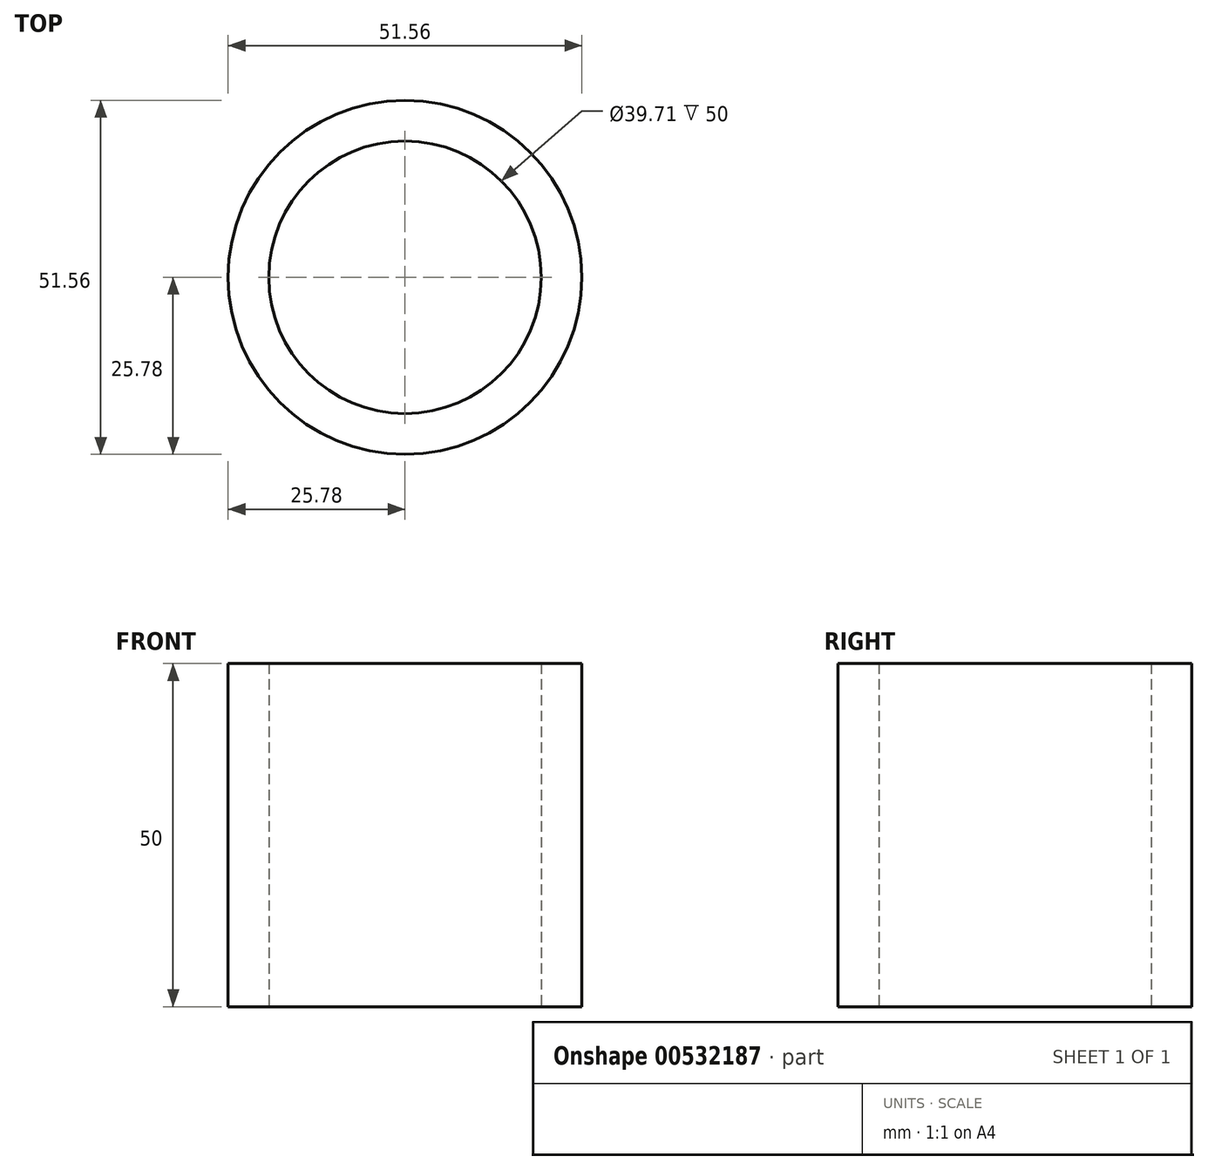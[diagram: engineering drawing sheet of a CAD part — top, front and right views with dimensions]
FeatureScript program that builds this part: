
annotation { "Feature Type Name" : "Feature", "Feature Type Description" : "" }
export const myFeature = defineFeature(function(context is Context, id is Id, definition is map)
    precondition{}
    {
        {
            var Q0;
            Q0=qCreatedBy(makeId("Top.planeOp"),FACE);
            var sketch = newSketch(context, id + "F0", { "sketchPlane" : qUnion([Q0])});
            skCircle(sketch, "E0", {"center": v(0, 0) * mm, "radius": 25.78 * mm});
            skSolve(sketch);
        }
        {
            var Q0;
            Q0 = qSketchRegion(id + "F0", true);
            extrude(context, id + "F1", {"entities" : qUnion([Q0]), "depth" : 50 * mm, "offsetDistance" : 25 * mm});
        }
        {
            var Q0;
            Q0=qCreatedBy(makeId("Top.planeOp"),FACE);
            var sketch = newSketch(context, id + "F2", { "sketchPlane" : qUnion([Q0])});
            skCircle(sketch, "E1", {"center": v(0, 0) * mm, "radius": 19.86 * mm});
            skSolve(sketch);
        }
        {
            var Q0;
            Q0=makeQuery(id+"F2.imprint","IMPRINT",FACE,{"disambiguationData":[TD([[makeQuery(id+"F2.imprint","IMPRINT",EDGE,{"derivedFrom":sQuery(id+"F2.wireOp",EDGE,"E1")}),1.0]])]});
            extrude(context, id + "F3", {"entities" : qUnion([Q0]), "operationType" : NewBodyOperationType.REMOVE, "depth" : 55 * mm, "offsetDistance" : 25 * mm});
        }
    });
